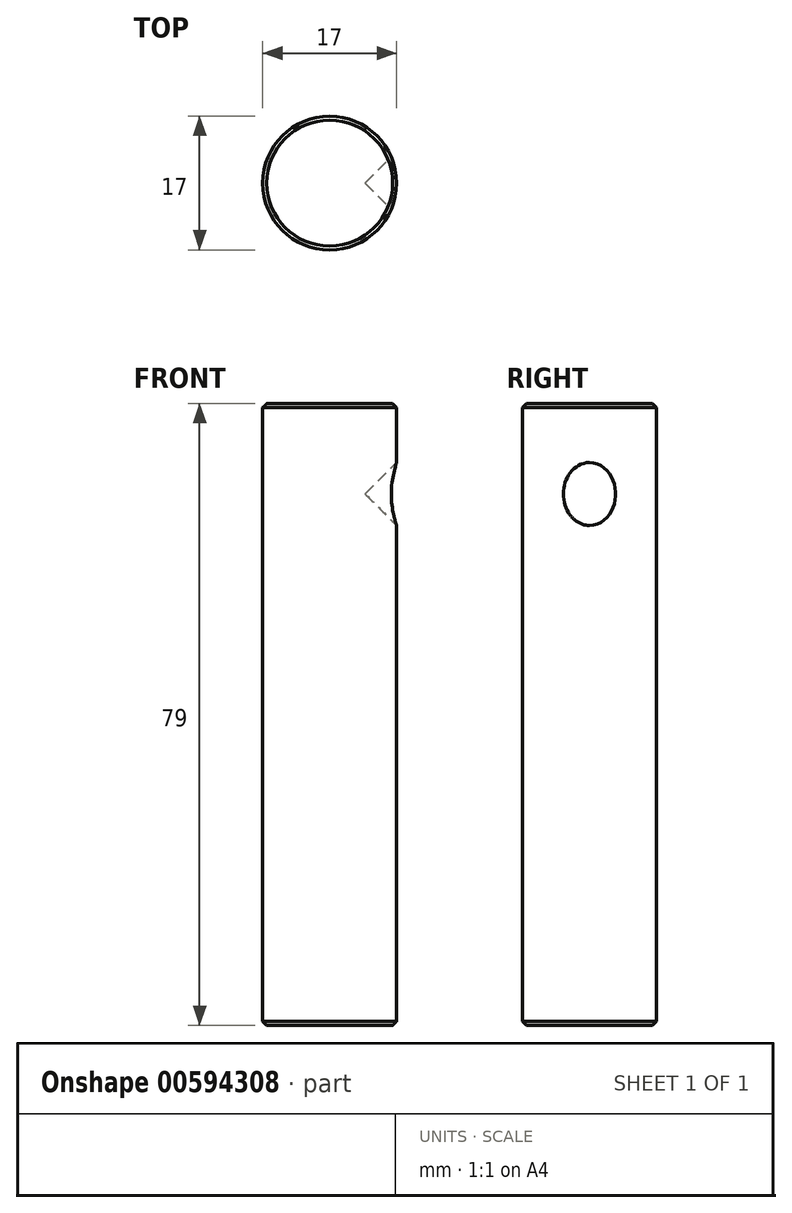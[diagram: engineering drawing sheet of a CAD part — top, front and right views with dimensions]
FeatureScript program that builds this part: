
annotation { "Feature Type Name" : "Feature", "Feature Type Description" : "" }
export const myFeature = defineFeature(function(context is Context, id is Id, definition is map)
    precondition{}
    {
        {
            var Q0;
            Q0=qCreatedBy(makeId("Front.planeOp"),FACE);
            var sketch = newSketch(context, id + "F0", { "sketchPlane" : qUnion([Q0])});
            skLineSegment(sketch, "E0", {"start": v(0, 0) * mm, "end": v(-8.5, 0) * mm});
            skLineSegment(sketch, "E1", {"start": v(-8.5, 0) * mm, "end": v(-8.5, 79) * mm});
            skLineSegment(sketch, "E2", {"start": v(-8.5, 79) * mm, "end": v(0, 79) * mm});
            skLineSegment(sketch, "E3", {"start": v(0, 79) * mm, "end": v(0, 0) * mm});
            skSolve(sketch);
        }
        {
            var Q0;
            Q0=makeQuery(id+"F0.imprint","IMPRINT",FACE,{"disambiguationData":[TD([[makeQuery(id+"F0.imprint","IMPRINT",EDGE,{"derivedFrom":sQuery(id+"F0.wireOp",EDGE,"E0")}),-1.0]])]});
            var Q1;
            Q1=sQuery(id+"F0.wireOp",EDGE,"E3");
            revolve(context, id + "F1", {"entities" : qUnion([Q0]), "axis" : qUnion([Q1]), "revolveType" : RevolveType.FULL});
        }
        {
            var Q0;
            Q0=qCreatedBy(makeId("Front.planeOp"),FACE);
            var sketch = newSketch(context, id + "F2", { "sketchPlane" : qUnion([Q0])});
            skLineSegment(sketch, "E4", {"start": v(-15.27, 67.5) * mm, "end": v(12.53, 67.5) * mm, "construction": true});
            skLineSegment(sketch, "E5", {"start": v(8.5, 79) * mm, "end": v(8.5, 0) * mm, "construction": true});
            skLineSegment(sketch, "E6", {"start": v(8.5, 67.5) * mm, "end": v(8.5, 71.5) * mm});
            skLineSegment(sketch, "E7", {"start": v(8.5, 71.5) * mm, "end": v(4.5, 67.5) * mm});
            skLineSegment(sketch, "E8", {"start": v(4.5, 67.5) * mm, "end": v(8.5, 67.5) * mm});
            skSolve(sketch);
        }
        {
            var Q0;
            Q0 = qSketchRegion(id + "F2", true);
            var Q1;
            Q1=sQuery(id+"F2.wireOp",EDGE,"E4");
            revolve(context, id + "F3", {"operationType" : NewBodyOperationType.REMOVE, "entities" : qUnion([Q0]), "axis" : qUnion([Q1]), "revolveType" : RevolveType.FULL, "oppositeDirection" : true});
        }
        {
            var Q0;
            Q0=makeQuery(id+"F1.opRevolve","SWEPT_EDGE",EDGE,{"disambiguationData":[OSD([sQuery(id+"F0.wireOp",EDGE,"E1"),sQuery(id+"F0.wireOp",EDGE,"E2")])]});
            var Q1;
            Q1=makeQuery(id+"F1.opRevolve","SWEPT_EDGE",EDGE,{"disambiguationData":[OSD([sQuery(id+"F0.wireOp",EDGE,"E0"),sQuery(id+"F0.wireOp",EDGE,"E1")])]});
            chamfer(context, id + "F4", {"entities" : qUnion([Q0, Q1]), "width" : .5 * mm, "tangentPropagation" : true});
        }
    });
